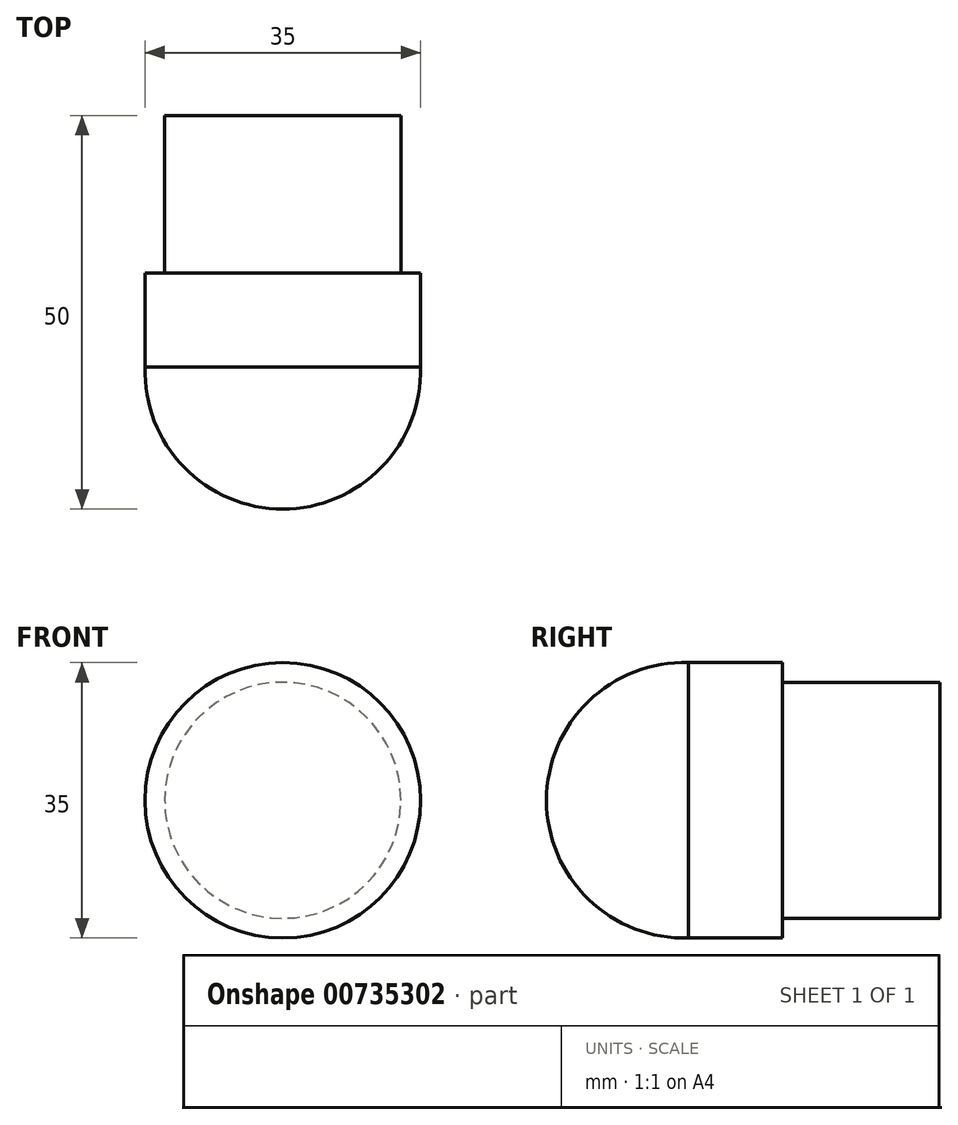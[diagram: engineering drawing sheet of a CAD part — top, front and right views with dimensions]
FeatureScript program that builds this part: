
annotation { "Feature Type Name" : "Feature", "Feature Type Description" : "" }
export const myFeature = defineFeature(function(context is Context, id is Id, definition is map)
    precondition{}
    {
        {
            var Q0;
            Q0=qCreatedBy(makeId("Right.planeOp"),FACE);
            var sketch = newSketch(context, id + "F0", { "sketchPlane" : qUnion([Q0])});
            skLineSegment(sketch, "E0", {"start": v(0, 0) * mm, "end": v(0, 15) * mm});
            skLineSegment(sketch, "E1", {"start": v(0, 15) * mm, "end": v(-20, 15) * mm});
            skLineSegment(sketch, "E2", {"start": v(-20, 17.5) * mm, "end": v(-20, 15) * mm});
            skLineSegment(sketch, "E3", {"start": v(-20, 17.5) * mm, "end": v(-31.96, 17.5) * mm});
            skArc(sketch, "E4", {"start": v(-31.96, 17.5) * mm, "mid": v(-44.68, 12.56) * mm, "end": v(-50, 0) * mm});
            skLineSegment(sketch, "E5", {"start": v(0, 0) * mm, "end": v(-50, 0) * mm});
            skSolve(sketch);
        }
        {
            var Q0;
            Q0=makeQuery(id+"F0.imprint","IMPRINT",FACE,{"disambiguationData":[TD([[makeQuery(id+"F0.imprint","IMPRINT",EDGE,{"derivedFrom":sQuery(id+"F0.wireOp",EDGE,"E0")}),1.0]])]});
            var Q1;
            Q1=sQuery(id+"F0.wireOp",EDGE,"E5");
            revolve(context, id + "F1", {"surfaceOperationType" : NewSurfaceOperationType.NEW, "entities" : qUnion([Q0]), "axis" : qUnion([Q1]), "revolveType" : RevolveType.FULL});
        }
    });
